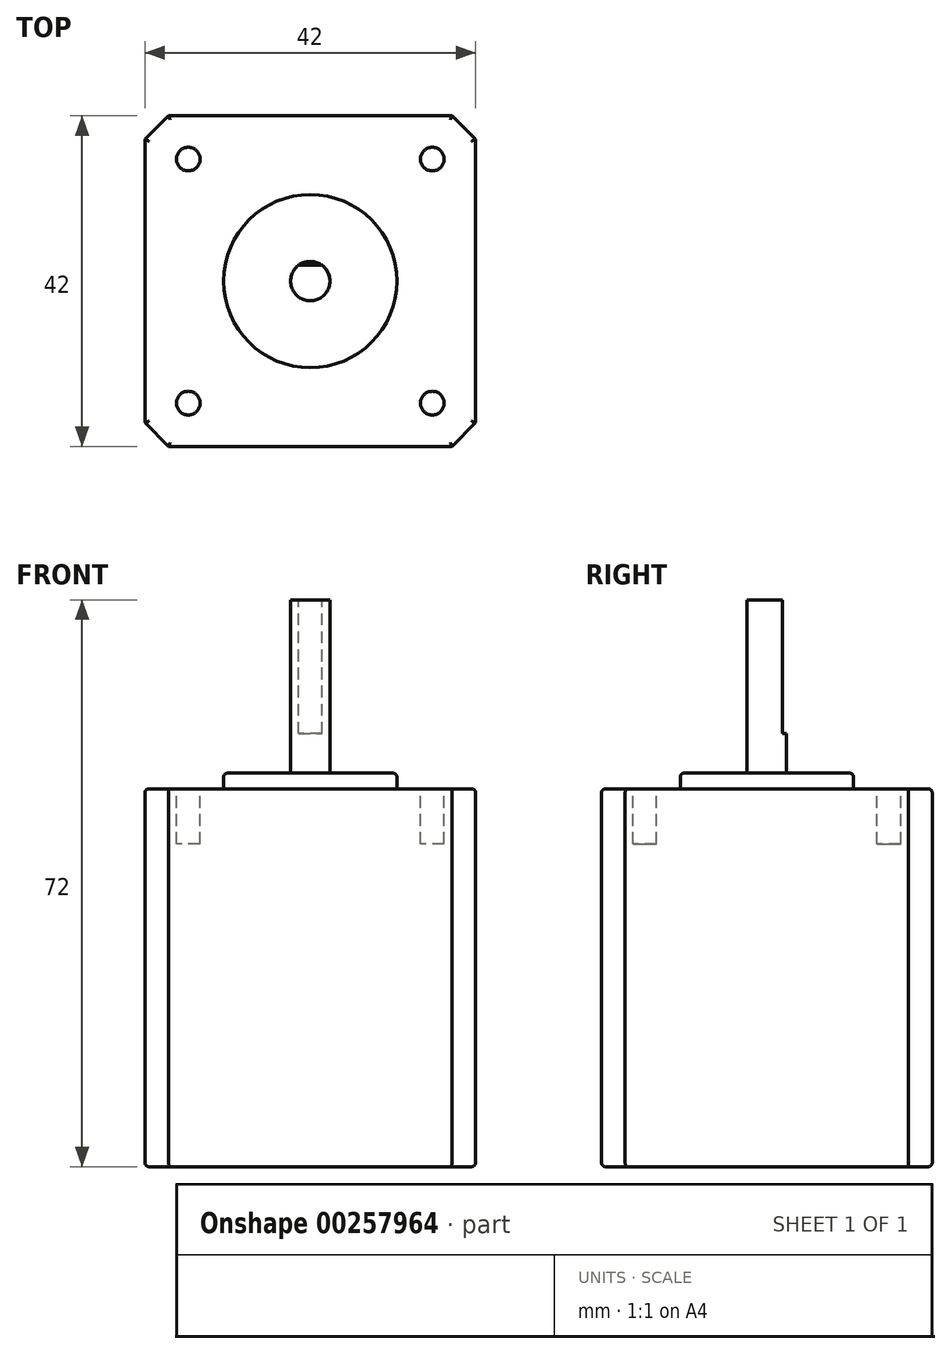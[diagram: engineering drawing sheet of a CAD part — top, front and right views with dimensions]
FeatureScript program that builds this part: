
annotation { "Feature Type Name" : "Feature", "Feature Type Description" : "" }
export const myFeature = defineFeature(function(context is Context, id is Id, definition is map)
    precondition{}
    {
        {
            assignVariable(context, id + "F0", {"name" : "height", "anyValue" : 48});
        }
        {
            assignVariable(context, id + "F1", {"name" : "shaft_length", "anyValue" : 22});
        }
        {
            var Q0;
            Q0=qCreatedBy(makeId("Top.planeOp"),FACE);
            var sketch = newSketch(context, id + "F2", { "sketchPlane" : qUnion([Q0])});
            skLineSegment(sketch, "E0.bottom", {"start": v(21, -21) * mm, "end": v(-21, -21) * mm});
            skLineSegment(sketch, "E0.top", {"start": v(21, 21) * mm, "end": v(-21, 21) * mm});
            skLineSegment(sketch, "E0.left", {"start": v(21, -21) * mm, "end": v(21, 21) * mm});
            skLineSegment(sketch, "E0.right", {"start": v(-21, -21) * mm, "end": v(-21, 21) * mm});
            skPoint(sketch, "E0.middle", {"position": v(0, 0) * mm});
            skSolve(sketch);
        }
        {
            var Q0;
            Q0=makeQuery(id+"F2.imprint","IMPRINT",FACE,{"disambiguationData":[TD([[makeQuery(id+"F2.imprint","IMPRINT",EDGE,{"derivedFrom":sQuery(id+"F2.wireOp",EDGE,"E0.bottom")}),-1.0]])]});
            extrude(context, id + "F3", {"entities" : qUnion([Q0]), "depth" : (getVariable(context, 'height')) * mm, "offsetDistance" : 25 * mm});
        }
        {
            var Q0;
            Q0=makeQuery(id+"F3.opExtrude","CAP_FACE",FACE,{"disambiguationData":[OSD([sQuery(id+"F2.wireOp",EDGE,"E0.bottom"),sQuery(id+"F2.wireOp",EDGE,"E0.top"),sQuery(id+"F2.wireOp",EDGE,"E0.left"),sQuery(id+"F2.wireOp",EDGE,"E0.right")])],"isStart":false});
            var sketch = newSketch(context, id + "F4", { "sketchPlane" : qUnion([Q0])});
            skLineSegment(sketch, "E1.bottom", {"start": v(15.5, 15.5) * mm, "end": v(-15.5, 15.5) * mm, "construction": true});
            skLineSegment(sketch, "E1.top", {"start": v(15.5, -15.5) * mm, "end": v(-15.5, -15.5) * mm, "construction": true});
            skLineSegment(sketch, "E1.left", {"start": v(15.5, 15.5) * mm, "end": v(15.5, -15.5) * mm, "construction": true});
            skLineSegment(sketch, "E1.right", {"start": v(-15.5, 15.5) * mm, "end": v(-15.5, -15.5) * mm, "construction": true});
            skPoint(sketch, "E1.middle", {"position": v(0, 0) * mm});
            skCircle(sketch, "E2", {"center": v(-15.5, 15.5) * mm, "radius": 1.5 * mm});
            skCircle(sketch, "E3", {"center": v(-15.5, -15.5) * mm, "radius": 1.5 * mm});
            skCircle(sketch, "E4", {"center": v(15.5, 15.5) * mm, "radius": 1.5 * mm});
            skCircle(sketch, "E5", {"center": v(15.5, -15.5) * mm, "radius": 1.5 * mm});
            skCircle(sketch, "E6", {"center": v(0, 0) * mm, "radius": 11 * mm});
            skSolve(sketch);
        }
        {
            var Q0;
            Q0=makeQuery(id+"F4.imprint","IMPRINT",FACE,{"disambiguationData":[TD([[makeQuery(id+"F4.imprint","IMPRINT",EDGE,{"derivedFrom":sQuery(id+"F4.wireOp",EDGE,"E3")}),1.0]])]});
            var Q1;
            Q1=makeQuery(id+"F4.imprint","IMPRINT",FACE,{"disambiguationData":[TD([[makeQuery(id+"F4.imprint","IMPRINT",EDGE,{"derivedFrom":sQuery(id+"F4.wireOp",EDGE,"E2")}),1.0]])]});
            var Q2;
            Q2=makeQuery(id+"F4.imprint","IMPRINT",FACE,{"disambiguationData":[TD([[makeQuery(id+"F4.imprint","IMPRINT",EDGE,{"derivedFrom":sQuery(id+"F4.wireOp",EDGE,"E4")}),1.0]])]});
            var Q3;
            Q3=makeQuery(id+"F4.imprint","IMPRINT",FACE,{"disambiguationData":[TD([[makeQuery(id+"F4.imprint","IMPRINT",EDGE,{"derivedFrom":sQuery(id+"F4.wireOp",EDGE,"E5")}),1.0]])]});
            var Q4;
            Q4=sQuery(id+"F4.wireOp",EDGE,"E2");
            var Q5;
            Q5=sQuery(id+"F4.wireOp",EDGE,"E3");
            var Q6;
            Q6=sQuery(id+"F4.wireOp",EDGE,"E5");
            var Q7;
            Q7=sQuery(id+"F4.wireOp",EDGE,"E4");
            extrude(context, id + "F5", {"entities" : qUnion([Q0, Q1, Q2, Q3]), "operationType" : NewBodyOperationType.REMOVE, "surfaceEntities" : qUnion([Q4, Q5, Q6, Q7]), "oppositeDirection" : true, "depth" : 7 * mm});
        }
        {
            var Q0;
            Q0=makeQuery(id+"F4.imprint","IMPRINT",FACE,{"disambiguationData":[TD([[makeQuery(id+"F4.imprint","IMPRINT",EDGE,{"derivedFrom":sQuery(id+"F4.wireOp",EDGE,"E6")}),1.0]])]});
            extrude(context, id + "F6", {"entities" : qUnion([Q0]), "operationType" : NewBodyOperationType.ADD, "depth" : 2 * mm});
        }
        {
            var Q0;
            Q0=makeQuery(id+"F6.opExtrude","CAP_FACE",FACE,{"disambiguationData":[OSD([sQuery(id+"F4.wireOp",EDGE,"E6")])],"isStart":false});
            var sketch = newSketch(context, id + "F7", { "sketchPlane" : qUnion([Q0])});
            skCircle(sketch, "E7", {"center": v(0, 0) * mm, "radius": 2.5 * mm});
            skSolve(sketch);
        }
        {
            var Q0;
            Q0=makeQuery(id+"F7.imprint","IMPRINT",FACE,{"disambiguationData":[TD([[makeQuery(id+"F7.imprint","IMPRINT",EDGE,{"derivedFrom":sQuery(id+"F7.wireOp",EDGE,"E7")}),1.0]])]});
            extrude(context, id + "F8", {"entities" : qUnion([Q0]), "operationType" : NewBodyOperationType.ADD, "depth" : (getVariable(context, 'shaft_length')) * mm});
        }
        {
            var Q0;
            Q0=makeQuery(id+"F8.opExtrude","CAP_FACE",FACE,{"disambiguationData":[OSD([sQuery(id+"F7.wireOp",EDGE,"E7")])],"isStart":false});
            var sketch = newSketch(context, id + "F9", { "sketchPlane" : qUnion([Q0])});
            skLineSegment(sketch, "E8", {"start": v(-1.5, 2) * mm, "end": v(1.5, 2) * mm});
            skSolve(sketch);
        }
        {
            var Q0;
            {var subQ0=sQuery(id+"F9.wireOp",EDGE,"E8");Q0=makeQuery(id+"F9.imprint","IMPRINT",FACE,{"disambiguationData":[TD([[makeQuery(id+"F9.imprint","IMPRINT",EDGE,{"derivedFrom":subQ0}),1.0]])]});}
            extrude(context, id + "F10", {"entities" : qUnion([Q0]), "operationType" : NewBodyOperationType.REMOVE, "oppositeDirection" : true, "depth" : (getVariable(context, 'shaft_length') - 5) * mm});
        }
        {
            var Q0;
            Q0=makeQuery(id+"F3.opExtrude","SWEPT_EDGE",EDGE,{"disambiguationData":[OSD([sQuery(id+"F2.wireOp",EDGE,"E0.bottom"),sQuery(id+"F2.wireOp",EDGE,"E0.left")])]});
            var Q1;
            Q1=makeQuery(id+"F3.opExtrude","SWEPT_EDGE",EDGE,{"disambiguationData":[OSD([sQuery(id+"F2.wireOp",EDGE,"E0.top"),sQuery(id+"F2.wireOp",EDGE,"E0.left")])]});
            var Q2;
            Q2=makeQuery(id+"F3.opExtrude","SWEPT_EDGE",EDGE,{"disambiguationData":[OSD([sQuery(id+"F2.wireOp",EDGE,"E0.bottom"),sQuery(id+"F2.wireOp",EDGE,"E0.right")])]});
            var Q3;
            Q3=makeQuery(id+"F3.opExtrude","SWEPT_EDGE",EDGE,{"disambiguationData":[OSD([sQuery(id+"F2.wireOp",EDGE,"E0.top"),sQuery(id+"F2.wireOp",EDGE,"E0.right")])]});
            chamfer(context, id + "F11", {"entities" : qUnion([Q0, Q1, Q2, Q3]), "width" : 3 * mm, "tangentPropagation" : true});
        }
        {
            var Q0;
            Q0=makeQuery(id+"F3.opExtrude","CAP_EDGE",EDGE,{"disambiguationData":[OSD([sQuery(id+"F2.wireOp",EDGE,"E0.top")])],"isStart":false});
            var Q1;
            {var subQ0=sQuery(id+"F2.wireOp",EDGE,"E0.left");var subQ1=sQuery(id+"F2.wireOp",EDGE,"E0.top");Q1=makeQuery(id+"F11.opChamfer","BLEND_EDGE",EDGE,{"blendedFrom":[makeQuery(id+"F3.opExtrude","SWEPT_EDGE",EDGE,{"disambiguationData":[OSD([subQ1,subQ0])]}),makeQuery(id+"F3.opExtrude","CAP_FACE",FACE,{"disambiguationData":[OSD([sQuery(id+"F2.wireOp",EDGE,"E0.bottom"),subQ1,subQ0,sQuery(id+"F2.wireOp",EDGE,"E0.right")])],"isStart":false})],"blendedInto":[makeQuery(id+"F3.opExtrude","CAP_FACE",FACE,{"disambiguationData":[OSD([sQuery(id+"F2.wireOp",EDGE,"E0.bottom"),subQ1,subQ0,sQuery(id+"F2.wireOp",EDGE,"E0.right")])],"isStart":false})]});}
            var Q2;
            Q2=makeQuery(id+"F3.opExtrude","CAP_EDGE",EDGE,{"disambiguationData":[OSD([sQuery(id+"F2.wireOp",EDGE,"E0.left")])],"isStart":false});
            var Q3;
            {var subQ0=sQuery(id+"F2.wireOp",EDGE,"E0.left");var subQ1=sQuery(id+"F2.wireOp",EDGE,"E0.bottom");Q3=makeQuery(id+"F11.opChamfer","BLEND_EDGE",EDGE,{"blendedFrom":[makeQuery(id+"F3.opExtrude","SWEPT_EDGE",EDGE,{"disambiguationData":[OSD([subQ1,subQ0])]}),makeQuery(id+"F3.opExtrude","CAP_FACE",FACE,{"disambiguationData":[OSD([subQ1,sQuery(id+"F2.wireOp",EDGE,"E0.top"),subQ0,sQuery(id+"F2.wireOp",EDGE,"E0.right")])],"isStart":false})],"blendedInto":[makeQuery(id+"F3.opExtrude","CAP_FACE",FACE,{"disambiguationData":[OSD([subQ1,sQuery(id+"F2.wireOp",EDGE,"E0.top"),subQ0,sQuery(id+"F2.wireOp",EDGE,"E0.right")])],"isStart":false})]});}
            var Q4;
            Q4=makeQuery(id+"F3.opExtrude","CAP_EDGE",EDGE,{"disambiguationData":[OSD([sQuery(id+"F2.wireOp",EDGE,"E0.bottom")])],"isStart":false});
            var Q5;
            {var subQ0=sQuery(id+"F2.wireOp",EDGE,"E0.right");var subQ1=sQuery(id+"F2.wireOp",EDGE,"E0.bottom");Q5=makeQuery(id+"F11.opChamfer","BLEND_EDGE",EDGE,{"blendedFrom":[makeQuery(id+"F3.opExtrude","SWEPT_EDGE",EDGE,{"disambiguationData":[OSD([subQ1,subQ0])]}),makeQuery(id+"F3.opExtrude","CAP_FACE",FACE,{"disambiguationData":[OSD([subQ1,sQuery(id+"F2.wireOp",EDGE,"E0.top"),sQuery(id+"F2.wireOp",EDGE,"E0.left"),subQ0])],"isStart":false})],"blendedInto":[makeQuery(id+"F3.opExtrude","CAP_FACE",FACE,{"disambiguationData":[OSD([subQ1,sQuery(id+"F2.wireOp",EDGE,"E0.top"),sQuery(id+"F2.wireOp",EDGE,"E0.left"),subQ0])],"isStart":false})]});}
            var Q6;
            Q6=makeQuery(id+"F3.opExtrude","CAP_EDGE",EDGE,{"disambiguationData":[OSD([sQuery(id+"F2.wireOp",EDGE,"E0.right")])],"isStart":false});
            var Q7;
            {var subQ0=sQuery(id+"F2.wireOp",EDGE,"E0.right");var subQ1=sQuery(id+"F2.wireOp",EDGE,"E0.top");Q7=makeQuery(id+"F11.opChamfer","BLEND_EDGE",EDGE,{"blendedFrom":[makeQuery(id+"F3.opExtrude","SWEPT_EDGE",EDGE,{"disambiguationData":[OSD([subQ1,subQ0])]}),makeQuery(id+"F3.opExtrude","CAP_FACE",FACE,{"disambiguationData":[OSD([sQuery(id+"F2.wireOp",EDGE,"E0.bottom"),subQ1,sQuery(id+"F2.wireOp",EDGE,"E0.left"),subQ0])],"isStart":false})],"blendedInto":[makeQuery(id+"F3.opExtrude","CAP_FACE",FACE,{"disambiguationData":[OSD([sQuery(id+"F2.wireOp",EDGE,"E0.bottom"),subQ1,sQuery(id+"F2.wireOp",EDGE,"E0.left"),subQ0])],"isStart":false})]});}
            fillet(context, id + "F12", {"entities" : qUnion([Q0, Q1, Q2, Q3, Q4, Q5, Q6, Q7]), "radius" : 0.5 * mm, "tangentPropagation" : true, "allowEdgeOverflow" : false});
        }
        {
            var Q0;
            {var subQ0=sQuery(id+"F2.wireOp",EDGE,"E0.right");var subQ1=sQuery(id+"F2.wireOp",EDGE,"E0.top");Q0=makeQuery(id+"F11.opChamfer","BLEND_EDGE",EDGE,{"blendedFrom":[makeQuery(id+"F3.opExtrude","SWEPT_EDGE",EDGE,{"disambiguationData":[OSD([subQ1,subQ0])]}),makeQuery(id+"F3.opExtrude","CAP_FACE",FACE,{"disambiguationData":[OSD([sQuery(id+"F2.wireOp",EDGE,"E0.bottom"),subQ1,sQuery(id+"F2.wireOp",EDGE,"E0.left"),subQ0])],"isStart":true})],"blendedInto":[makeQuery(id+"F3.opExtrude","CAP_FACE",FACE,{"disambiguationData":[OSD([sQuery(id+"F2.wireOp",EDGE,"E0.bottom"),subQ1,sQuery(id+"F2.wireOp",EDGE,"E0.left"),subQ0])],"isStart":true})]});}
            var Q1;
            Q1=makeQuery(id+"F3.opExtrude","CAP_EDGE",EDGE,{"disambiguationData":[OSD([sQuery(id+"F2.wireOp",EDGE,"E0.top")])],"isStart":true});
            var Q2;
            {var subQ0=sQuery(id+"F2.wireOp",EDGE,"E0.left");var subQ1=sQuery(id+"F2.wireOp",EDGE,"E0.top");Q2=makeQuery(id+"F11.opChamfer","BLEND_EDGE",EDGE,{"blendedFrom":[makeQuery(id+"F3.opExtrude","SWEPT_EDGE",EDGE,{"disambiguationData":[OSD([subQ1,subQ0])]}),makeQuery(id+"F3.opExtrude","CAP_FACE",FACE,{"disambiguationData":[OSD([sQuery(id+"F2.wireOp",EDGE,"E0.bottom"),subQ1,subQ0,sQuery(id+"F2.wireOp",EDGE,"E0.right")])],"isStart":true})],"blendedInto":[makeQuery(id+"F3.opExtrude","CAP_FACE",FACE,{"disambiguationData":[OSD([sQuery(id+"F2.wireOp",EDGE,"E0.bottom"),subQ1,subQ0,sQuery(id+"F2.wireOp",EDGE,"E0.right")])],"isStart":true})]});}
            var Q3;
            Q3=makeQuery(id+"F3.opExtrude","CAP_EDGE",EDGE,{"disambiguationData":[OSD([sQuery(id+"F2.wireOp",EDGE,"E0.left")])],"isStart":true});
            var Q4;
            {var subQ0=sQuery(id+"F2.wireOp",EDGE,"E0.left");var subQ1=sQuery(id+"F2.wireOp",EDGE,"E0.bottom");Q4=makeQuery(id+"F11.opChamfer","BLEND_EDGE",EDGE,{"blendedFrom":[makeQuery(id+"F3.opExtrude","SWEPT_EDGE",EDGE,{"disambiguationData":[OSD([subQ1,subQ0])]}),makeQuery(id+"F3.opExtrude","CAP_FACE",FACE,{"disambiguationData":[OSD([subQ1,sQuery(id+"F2.wireOp",EDGE,"E0.top"),subQ0,sQuery(id+"F2.wireOp",EDGE,"E0.right")])],"isStart":true})],"blendedInto":[makeQuery(id+"F3.opExtrude","CAP_FACE",FACE,{"disambiguationData":[OSD([subQ1,sQuery(id+"F2.wireOp",EDGE,"E0.top"),subQ0,sQuery(id+"F2.wireOp",EDGE,"E0.right")])],"isStart":true})]});}
            var Q5;
            Q5=makeQuery(id+"F3.opExtrude","CAP_EDGE",EDGE,{"disambiguationData":[OSD([sQuery(id+"F2.wireOp",EDGE,"E0.bottom")])],"isStart":true});
            var Q6;
            {var subQ0=sQuery(id+"F2.wireOp",EDGE,"E0.right");var subQ1=sQuery(id+"F2.wireOp",EDGE,"E0.bottom");Q6=makeQuery(id+"F11.opChamfer","BLEND_EDGE",EDGE,{"blendedFrom":[makeQuery(id+"F3.opExtrude","SWEPT_EDGE",EDGE,{"disambiguationData":[OSD([subQ1,subQ0])]}),makeQuery(id+"F3.opExtrude","CAP_FACE",FACE,{"disambiguationData":[OSD([subQ1,sQuery(id+"F2.wireOp",EDGE,"E0.top"),sQuery(id+"F2.wireOp",EDGE,"E0.left"),subQ0])],"isStart":true})],"blendedInto":[makeQuery(id+"F3.opExtrude","CAP_FACE",FACE,{"disambiguationData":[OSD([subQ1,sQuery(id+"F2.wireOp",EDGE,"E0.top"),sQuery(id+"F2.wireOp",EDGE,"E0.left"),subQ0])],"isStart":true})]});}
            var Q7;
            Q7=makeQuery(id+"F3.opExtrude","CAP_EDGE",EDGE,{"disambiguationData":[OSD([sQuery(id+"F2.wireOp",EDGE,"E0.right")])],"isStart":true});
            fillet(context, id + "F13", {"entities" : qUnion([Q0, Q1, Q2, Q3, Q4, Q5, Q6, Q7]), "radius" : 0.5 * mm, "tangentPropagation" : true, "allowEdgeOverflow" : false});
        }
        {
            var Q0;
            Q0=makeQuery(id+"F6.opExtrude","CAP_EDGE",EDGE,{"disambiguationData":[OSD([sQuery(id+"F4.wireOp",EDGE,"E6")])],"isStart":false});
            fillet(context, id + "F14", {"entities" : qUnion([Q0]), "radius" : 0.5 * mm, "tangentPropagation" : true, "allowEdgeOverflow" : false});
        }
    });
